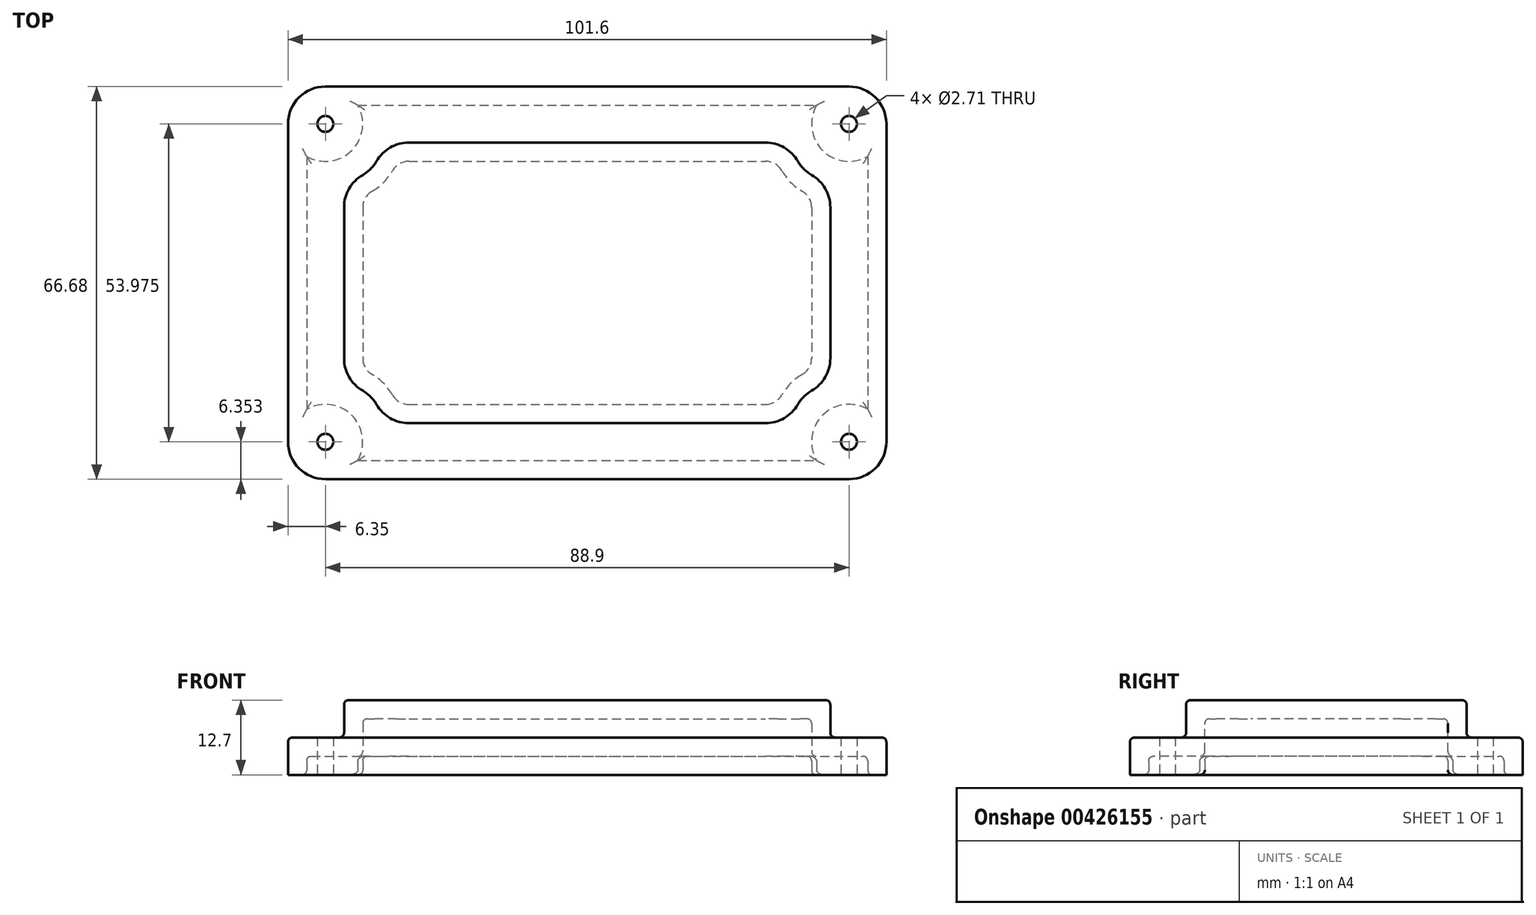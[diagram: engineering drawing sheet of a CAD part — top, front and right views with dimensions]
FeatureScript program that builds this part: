
annotation { "Feature Type Name" : "Feature", "Feature Type Description" : "" }
export const myFeature = defineFeature(function(context is Context, id is Id, definition is map)
    precondition{}
    {
        {
            var Q0;
            Q0=qCreatedBy(makeId("Top.planeOp"),FACE);
            var sketch = newSketch(context, id + "F0", { "sketchPlane" : qUnion([Q0])});
            skLineSegment(sketch, "E0.bottom", {"start": v(-44.45, 33.34) * mm, "end": v(44.45, 33.34) * mm});
            skLineSegment(sketch, "E0.top", {"start": v(-44.45, -33.34) * mm, "end": v(44.45, -33.34) * mm});
            skLineSegment(sketch, "E0.left", {"start": v(-50.8, 26.99) * mm, "end": v(-50.8, -26.99) * mm});
            skLineSegment(sketch, "E0.right", {"start": v(50.8, 26.99) * mm, "end": v(50.8, -26.99) * mm});
            skPoint(sketch, "E0.middle", {"position": v(0, 0) * mm});
            skPoint(sketch, "E1.visualSharp", {"position": v(-50.8, 33.34) * mm});
            skArc(sketch, "E1.filletArc", {"start": v(-44.45, 33.34) * mm, "mid": v(-48.94, 31.48) * mm, "end": v(-50.8, 26.99) * mm});
            skPoint(sketch, "E2.visualSharp", {"position": v(-50.8, -33.34) * mm});
            skArc(sketch, "E2.filletArc", {"start": v(-50.8, -26.99) * mm, "mid": v(-48.94, -31.48) * mm, "end": v(-44.45, -33.34) * mm});
            skPoint(sketch, "E3.visualSharp", {"position": v(50.8, -33.34) * mm});
            skArc(sketch, "E3.filletArc", {"start": v(44.45, -33.34) * mm, "mid": v(48.94, -31.48) * mm, "end": v(50.8, -26.99) * mm});
            skPoint(sketch, "E4.visualSharp", {"position": v(50.8, 33.34) * mm});
            skArc(sketch, "E4.filletArc", {"start": v(50.8, 26.99) * mm, "mid": v(48.94, 31.48) * mm, "end": v(44.45, 33.34) * mm});
            skSolve(sketch);
        }
        {
            var Q0;
            Q0 = qSketchRegion(id + "F0", true);
            extrude(context, id + "F1", {"entities" : qUnion([Q0]), "depth" : 6.35 * mm});
        }
        {
            var Q0;
            Q0=makeQuery(id+"F1.opExtrude","CAP_FACE",FACE,{"disambiguationData":[OSD([sQuery(id+"F0.wireOp",EDGE,"E0.bottom"),sQuery(id+"F0.wireOp",EDGE,"E0.top"),sQuery(id+"F0.wireOp",EDGE,"E0.left"),sQuery(id+"F0.wireOp",EDGE,"E0.right"),sQuery(id+"F0.wireOp",EDGE,"E1.filletArc"),sQuery(id+"F0.wireOp",EDGE,"E2.filletArc"),sQuery(id+"F0.wireOp",EDGE,"E3.filletArc"),sQuery(id+"F0.wireOp",EDGE,"E4.filletArc")])],"isStart":false});
            var sketch = newSketch(context, id + "F2", { "sketchPlane" : qUnion([Q0])});
            skLineSegment(sketch, "E5.0", {"start": v(-41.27, 23.81) * mm, "end": v(-41.28, -23.81) * mm});
            skLineSegment(sketch, "E5.1", {"start": v(-41.27, 23.81) * mm, "end": v(41.28, 23.81) * mm});
            skLineSegment(sketch, "E5.2", {"start": v(41.28, 23.81) * mm, "end": v(41.27, -23.81) * mm});
            skLineSegment(sketch, "E5.3", {"start": v(-41.28, -23.81) * mm, "end": v(41.27, -23.81) * mm});
            skSolve(sketch);
        }
        {
            var Q0;
            Q0 = qSketchRegion(id + "F2", true);
            extrude(context, id + "F3", {"entities" : qUnion([Q0]), "operationType" : NewBodyOperationType.ADD, "depth" : 6.35 * mm});
        }
        {
            var Q0;
            Q0=makeQuery(id+"F3.opExtrude","CAP_FACE",FACE,{"disambiguationData":[OSD([sQuery(id+"F2.wireOp",EDGE,"E5.0"),sQuery(id+"F2.wireOp",EDGE,"E5.1"),sQuery(id+"F2.wireOp",EDGE,"E5.2"),sQuery(id+"F2.wireOp",EDGE,"E5.3")])],"isStart":false});
            var sketch = newSketch(context, id + "F4", { "sketchPlane" : qUnion([Q0])});
            skLineSegment(sketch, "E6", {"start": v(0, 23.81) * mm, "end": v(0, 0) * mm, "construction": true});
            skLineSegment(sketch, "E7", {"start": v(0, 0) * mm, "end": v(41.28, 0) * mm, "construction": true});
            skCircle(sketch, "E8", {"center": v(41.28, 23.81) * mm, "radius": 6.35 * mm});
            skCircle(sketch, "E9.MirrorC", {"center": v(41.28, -23.81) * mm, "radius": 6.35 * mm});
            skSolve(sketch);
        }
        {
            var Q0;
            Q0 = qSketchRegion(id + "F4", true);
            var Q1;
            Q1=makeQuery(id+"F1.opExtrude","CAP_FACE",FACE,{"disambiguationData":[OSD([sQuery(id+"F0.wireOp",EDGE,"E0.bottom"),sQuery(id+"F0.wireOp",EDGE,"E0.top"),sQuery(id+"F0.wireOp",EDGE,"E0.left"),sQuery(id+"F0.wireOp",EDGE,"E0.right"),sQuery(id+"F0.wireOp",EDGE,"E1.filletArc"),sQuery(id+"F0.wireOp",EDGE,"E2.filletArc"),sQuery(id+"F0.wireOp",EDGE,"E3.filletArc"),sQuery(id+"F0.wireOp",EDGE,"E4.filletArc")])],"isStart":false});
            extrude(context, id + "F5", {"entities" : qUnion([Q0]), "operationType" : NewBodyOperationType.REMOVE, "endBound" : BoundingType.UP_TO_SURFACE, "oppositeDirection" : true, "endBoundEntityFace" : qUnion([Q1]), "depth" : 25.4 * mm});
        }
        {
            var Q0;
            Q0=makeQuery(id+"F3.opExtrude","CAP_FACE",FACE,{"disambiguationData":[OSD([sQuery(id+"F2.wireOp",EDGE,"E5.0"),sQuery(id+"F2.wireOp",EDGE,"E5.1"),sQuery(id+"F2.wireOp",EDGE,"E5.2"),sQuery(id+"F2.wireOp",EDGE,"E5.3")])],"isStart":false});
            var sketch = newSketch(context, id + "F6", { "sketchPlane" : qUnion([Q0])});
            skLineSegment(sketch, "E10", {"start": v(0, 23.81) * mm, "end": v(0, 0) * mm, "construction": true});
            skLineSegment(sketch, "E11", {"start": v(0, 0) * mm, "end": v(-41.28, 0) * mm, "construction": true});
            skCircle(sketch, "E12", {"center": v(-41.27, 23.81) * mm, "radius": 6.35 * mm});
            skCircle(sketch, "E13.MirrorC", {"center": v(-41.27, -23.81) * mm, "radius": 6.35 * mm});
            skSolve(sketch);
        }
        {
            var Q0;
            Q0 = qSketchRegion(id + "F6", true);
            var Q1;
            {var subQ0=sQuery(id+"F4.wireOp",EDGE,"E9.MirrorC");var subQ1=makeQuery(id+"F3.opExtrude","CAP_EDGE",EDGE,{"disambiguationData":[OSD([sQuery(id+"F2.wireOp",EDGE,"E5.2")])],"isStart":false});var subQ2=sQuery(id+"F0.wireOp",EDGE,"E4.filletArc");var subQ3=sQuery(id+"F0.wireOp",EDGE,"E3.filletArc");var subQ4=sQuery(id+"F0.wireOp",EDGE,"E2.filletArc");var subQ5=sQuery(id+"F0.wireOp",EDGE,"E1.filletArc");var subQ6=sQuery(id+"F0.wireOp",EDGE,"E0.right");var subQ7=sQuery(id+"F0.wireOp",EDGE,"E0.left");var subQ8=sQuery(id+"F0.wireOp",EDGE,"E0.top");var subQ9=sQuery(id+"F0.wireOp",EDGE,"E0.bottom");var subQ10=sQuery(id+"F4.wireOp",EDGE,"E8");Q1=makeQuery(id+"F5.boolean.opBoolean","MERGE",FACE,{"derivedFrom":[makeQuery(id+"F1.opExtrude","CAP_FACE",FACE,{"disambiguationData":[OSD([subQ9,subQ8,subQ7,subQ6,subQ5,subQ4,subQ3,subQ2])],"isStart":false}),makeQuery(id+"F5.opExtrude","CAP_FACE",FACE,{"disambiguationData":[OSD([subQ9,subQ8,subQ7,subQ6,subQ5,subQ4,subQ3,subQ2]),ownerDisambiguation([makeQuery(id+"F4.imprint","IMPRINT",EDGE,{"disambiguationData":[TD([[makeQuery(id+"F4.imprint","INTERSECT",VERTEX,{"derivedFrom":[makeQuery(id+"F3.opExtrude","CAP_EDGE",EDGE,{"disambiguationData":[OSD([sQuery(id+"F2.wireOp",EDGE,"E5.1")])],"isStart":false}),subQ10]}),-1.0]])],"derivedFrom":subQ10})])],"isStart":false}),makeQuery(id+"F5.opExtrude","CAP_FACE",FACE,{"disambiguationData":[OSD([subQ9,subQ8,subQ7,subQ6,subQ5,subQ4,subQ3,subQ2]),ownerDisambiguation([makeQuery(id+"F4.imprint","IMPRINT",EDGE,{"disambiguationData":[TD([[makeQuery(id+"F4.imprint","INTERSECT",VERTEX,{"derivedFrom":[subQ1,subQ0]}),1.0]])],"derivedFrom":subQ0})])],"isStart":false})]});}
            extrude(context, id + "F7", {"entities" : qUnion([Q0]), "operationType" : NewBodyOperationType.REMOVE, "endBound" : BoundingType.UP_TO_SURFACE, "oppositeDirection" : true, "endBoundEntityFace" : qUnion([Q1]), "depth" : 25.4 * mm});
        }
        {
            var Q0;
            Q0=makeQuery(id+"F7.boolean.opBoolean","INTERSECT",EDGE,{"derivedFrom":[makeQuery(id+"F3.opExtrude","SWEPT_FACE",FACE,{"disambiguationData":[OSD([sQuery(id+"F2.wireOp",EDGE,"E5.3")])]}),makeQuery(id+"F7.opExtrude","SWEPT_FACE",FACE,{"disambiguationData":[OSD([sQuery(id+"F6.wireOp",EDGE,"E13.MirrorC")])]})]});
            var Q1;
            Q1=makeQuery(id+"F7.boolean.opBoolean","INTERSECT",EDGE,{"derivedFrom":[makeQuery(id+"F3.opExtrude","SWEPT_FACE",FACE,{"disambiguationData":[OSD([sQuery(id+"F2.wireOp",EDGE,"E5.0")])]}),makeQuery(id+"F7.opExtrude","SWEPT_FACE",FACE,{"disambiguationData":[OSD([sQuery(id+"F6.wireOp",EDGE,"E13.MirrorC")])]})]});
            var Q2;
            Q2=makeQuery(id+"F7.boolean.opBoolean","INTERSECT",EDGE,{"derivedFrom":[makeQuery(id+"F3.opExtrude","SWEPT_FACE",FACE,{"disambiguationData":[OSD([sQuery(id+"F2.wireOp",EDGE,"E5.0")])]}),makeQuery(id+"F7.opExtrude","SWEPT_FACE",FACE,{"disambiguationData":[OSD([sQuery(id+"F6.wireOp",EDGE,"E12")])]})]});
            var Q3;
            Q3=makeQuery(id+"F7.boolean.opBoolean","INTERSECT",EDGE,{"derivedFrom":[makeQuery(id+"F3.opExtrude","SWEPT_FACE",FACE,{"disambiguationData":[OSD([sQuery(id+"F2.wireOp",EDGE,"E5.1")])]}),makeQuery(id+"F7.opExtrude","SWEPT_FACE",FACE,{"disambiguationData":[OSD([sQuery(id+"F6.wireOp",EDGE,"E12")])]})]});
            var Q4;
            Q4=makeQuery(id+"F5.boolean.opBoolean","INTERSECT",EDGE,{"derivedFrom":[makeQuery(id+"F3.opExtrude","SWEPT_FACE",FACE,{"disambiguationData":[OSD([sQuery(id+"F2.wireOp",EDGE,"E5.1")])]}),makeQuery(id+"F5.opExtrude","SWEPT_FACE",FACE,{"disambiguationData":[OSD([sQuery(id+"F4.wireOp",EDGE,"E8")])]})]});
            var Q5;
            Q5=makeQuery(id+"F5.boolean.opBoolean","INTERSECT",EDGE,{"derivedFrom":[makeQuery(id+"F3.opExtrude","SWEPT_FACE",FACE,{"disambiguationData":[OSD([sQuery(id+"F2.wireOp",EDGE,"E5.2")])]}),makeQuery(id+"F5.opExtrude","SWEPT_FACE",FACE,{"disambiguationData":[OSD([sQuery(id+"F4.wireOp",EDGE,"E8")])]})]});
            var Q6;
            Q6=makeQuery(id+"F5.boolean.opBoolean","INTERSECT",EDGE,{"derivedFrom":[makeQuery(id+"F3.opExtrude","SWEPT_FACE",FACE,{"disambiguationData":[OSD([sQuery(id+"F2.wireOp",EDGE,"E5.2")])]}),makeQuery(id+"F5.opExtrude","SWEPT_FACE",FACE,{"disambiguationData":[OSD([sQuery(id+"F4.wireOp",EDGE,"E9.MirrorC")])]})]});
            var Q7;
            Q7=makeQuery(id+"F5.boolean.opBoolean","INTERSECT",EDGE,{"derivedFrom":[makeQuery(id+"F3.opExtrude","SWEPT_FACE",FACE,{"disambiguationData":[OSD([sQuery(id+"F2.wireOp",EDGE,"E5.3")])]}),makeQuery(id+"F5.opExtrude","SWEPT_FACE",FACE,{"disambiguationData":[OSD([sQuery(id+"F4.wireOp",EDGE,"E9.MirrorC")])]})]});
            fillet(context, id + "F8", {"entities" : qUnion([Q0, Q1, Q2, Q3, Q4, Q5, Q6, Q7]), "radius" : 6.35 * mm, "tangentPropagation" : true, "allowEdgeOverflow" : false});
        }
        {
            var Q0;
            Q0=makeQuery(id+"F1.opExtrude","CAP_FACE",FACE,{"disambiguationData":[OSD([sQuery(id+"F0.wireOp",EDGE,"E0.bottom"),sQuery(id+"F0.wireOp",EDGE,"E0.top"),sQuery(id+"F0.wireOp",EDGE,"E0.left"),sQuery(id+"F0.wireOp",EDGE,"E0.right"),sQuery(id+"F0.wireOp",EDGE,"E1.filletArc"),sQuery(id+"F0.wireOp",EDGE,"E2.filletArc"),sQuery(id+"F0.wireOp",EDGE,"E3.filletArc"),sQuery(id+"F0.wireOp",EDGE,"E4.filletArc")])],"isStart":true});
            shell(context, id + "F9", {"entities" : qUnion([Q0]), "thickness" : 3.17 * mm});
        }
        {
            var Q0;
            Q0=makeQuery(id+"F1.opExtrude","CAP_FACE",FACE,{"disambiguationData":[OSD([sQuery(id+"F0.wireOp",EDGE,"E0.bottom"),sQuery(id+"F0.wireOp",EDGE,"E0.top"),sQuery(id+"F0.wireOp",EDGE,"E0.left"),sQuery(id+"F0.wireOp",EDGE,"E0.right"),sQuery(id+"F0.wireOp",EDGE,"E1.filletArc"),sQuery(id+"F0.wireOp",EDGE,"E2.filletArc"),sQuery(id+"F0.wireOp",EDGE,"E3.filletArc"),sQuery(id+"F0.wireOp",EDGE,"E4.filletArc")])],"isStart":true});
            var sketch = newSketch(context, id + "F10", { "sketchPlane" : qUnion([Q0])});
            skCircle(sketch, "E14", {"center": v(44.45, 26.99) * mm, "radius": 6.35 * mm});
            skCircle(sketch, "E15", {"center": v(44.45, -26.99) * mm, "radius": 6.35 * mm});
            skCircle(sketch, "E16", {"center": v(-44.45, -26.99) * mm, "radius": 6.35 * mm});
            skCircle(sketch, "E17", {"center": v(-44.45, 26.99) * mm, "radius": 6.35 * mm});
            skSolve(sketch);
        }
        {
            var Q0;
            Q0 = qSketchRegion(id + "F10", true);
            var Q1;
            Q1=makeQuery(id+"F9.opShell","OFFSET_FACE",FACE,{"disambiguationData":[OSD([sQuery(id+"F0.wireOp",EDGE,"E0.bottom"),sQuery(id+"F0.wireOp",EDGE,"E0.top"),sQuery(id+"F0.wireOp",EDGE,"E0.left"),sQuery(id+"F0.wireOp",EDGE,"E0.right"),sQuery(id+"F0.wireOp",EDGE,"E1.filletArc"),sQuery(id+"F0.wireOp",EDGE,"E2.filletArc"),sQuery(id+"F0.wireOp",EDGE,"E3.filletArc"),sQuery(id+"F0.wireOp",EDGE,"E4.filletArc")])]});
            extrude(context, id + "F11", {"entities" : qUnion([Q0]), "operationType" : NewBodyOperationType.ADD, "endBound" : BoundingType.UP_TO_SURFACE, "oppositeDirection" : true, "endBoundEntityFace" : qUnion([Q1]), "depth" : 4.57 * mm});
        }
        {
            var Q0;
            Q0=makeQuery(id+"F9.opShell","OFFSET_FACE",FACE,{"disambiguationData":[OSD([sQuery(id+"F0.wireOp",EDGE,"E0.bottom"),sQuery(id+"F0.wireOp",EDGE,"E0.top"),sQuery(id+"F0.wireOp",EDGE,"E0.left"),sQuery(id+"F0.wireOp",EDGE,"E0.right"),sQuery(id+"F0.wireOp",EDGE,"E1.filletArc"),sQuery(id+"F0.wireOp",EDGE,"E2.filletArc"),sQuery(id+"F0.wireOp",EDGE,"E3.filletArc"),sQuery(id+"F0.wireOp",EDGE,"E4.filletArc")])]});
            var Q1;
            Q1=makeQuery(id+"F9.opShell","OFFSET_FACE",FACE,{"disambiguationData":[OSD([sQuery(id+"F2.wireOp",EDGE,"E5.0"),sQuery(id+"F2.wireOp",EDGE,"E5.1"),sQuery(id+"F2.wireOp",EDGE,"E5.2"),sQuery(id+"F2.wireOp",EDGE,"E5.3")])]});
            var Q2;
            {var subQ0=sQuery(id+"F0.wireOp",EDGE,"E0.left");Q2=makeQuery(id+"F9.opShell","OFFSET_EDGE",EDGE,{"disambiguationData":[OSD([subQ0]),TDD([makeQuery(id+"F1.opExtrude","CAP_EDGE",EDGE,{"disambiguationData":[OSD([subQ0])],"isStart":true})])]});}
            var Q3;
            {var subQ0=sQuery(id+"F0.wireOp",EDGE,"E0.bottom");Q3=makeQuery(id+"F9.opShell","OFFSET_EDGE",EDGE,{"disambiguationData":[OSD([subQ0]),TDD([makeQuery(id+"F1.opExtrude","CAP_EDGE",EDGE,{"disambiguationData":[OSD([subQ0])],"isStart":true})])]});}
            var Q4;
            {var subQ0=sQuery(id+"F0.wireOp",EDGE,"E0.right");Q4=makeQuery(id+"F9.opShell","OFFSET_EDGE",EDGE,{"disambiguationData":[OSD([subQ0]),TDD([makeQuery(id+"F1.opExtrude","CAP_EDGE",EDGE,{"disambiguationData":[OSD([subQ0])],"isStart":true})])]});}
            var Q5;
            Q5=makeQuery(id+"F11.opExtrude","CAP_EDGE",EDGE,{"disambiguationData":[OSD([sQuery(id+"F10.wireOp",EDGE,"E15")])],"isStart":true});
            var Q6;
            Q6=makeQuery(id+"F11.opExtrude","CAP_EDGE",EDGE,{"disambiguationData":[OSD([sQuery(id+"F10.wireOp",EDGE,"E14")])],"isStart":true});
            var Q7;
            {var subQ0=sQuery(id+"F0.wireOp",EDGE,"E0.top");Q7=makeQuery(id+"F9.opShell","OFFSET_EDGE",EDGE,{"disambiguationData":[OSD([subQ0]),TDD([makeQuery(id+"F1.opExtrude","CAP_EDGE",EDGE,{"disambiguationData":[OSD([subQ0])],"isStart":true})])]});}
            var Q8;
            Q8=makeQuery(id+"F11.opExtrude","CAP_EDGE",EDGE,{"disambiguationData":[OSD([sQuery(id+"F10.wireOp",EDGE,"E17")])],"isStart":true});
            var Q9;
            Q9=makeQuery(id+"F3.opExtrude","CAP_FACE",FACE,{"disambiguationData":[OSD([sQuery(id+"F2.wireOp",EDGE,"E5.0"),sQuery(id+"F2.wireOp",EDGE,"E5.1"),sQuery(id+"F2.wireOp",EDGE,"E5.2"),sQuery(id+"F2.wireOp",EDGE,"E5.3")])],"isStart":false});
            var Q10;
            {var subQ0=sQuery(id+"F6.wireOp",EDGE,"E13.MirrorC");var subQ1=makeQuery(id+"F3.opExtrude","CAP_EDGE",EDGE,{"disambiguationData":[OSD([sQuery(id+"F2.wireOp",EDGE,"E5.0")])],"isStart":false});var subQ3=sQuery(id+"F0.wireOp",EDGE,"E4.filletArc");var subQ4=sQuery(id+"F0.wireOp",EDGE,"E3.filletArc");var subQ5=sQuery(id+"F0.wireOp",EDGE,"E2.filletArc");var subQ6=sQuery(id+"F0.wireOp",EDGE,"E1.filletArc");var subQ7=sQuery(id+"F0.wireOp",EDGE,"E0.right");var subQ8=sQuery(id+"F0.wireOp",EDGE,"E0.left");var subQ9=sQuery(id+"F0.wireOp",EDGE,"E0.top");var subQ10=sQuery(id+"F0.wireOp",EDGE,"E0.bottom");var subQ11=sQuery(id+"F6.wireOp",EDGE,"E12");var subQ12=makeQuery(id+"F3.opExtrude","CAP_EDGE",EDGE,{"disambiguationData":[OSD([sQuery(id+"F2.wireOp",EDGE,"E5.1")])],"isStart":false});var subQ13=sQuery(id+"F4.wireOp",EDGE,"E9.MirrorC");var subQ14=makeQuery(id+"F3.opExtrude","CAP_EDGE",EDGE,{"disambiguationData":[OSD([sQuery(id+"F2.wireOp",EDGE,"E5.2")])],"isStart":false});var subQ15=sQuery(id+"F4.wireOp",EDGE,"E8");Q10=makeQuery(id+"F7.boolean.opBoolean","MERGE",FACE,{"derivedFrom":[makeQuery(id+"F5.boolean.opBoolean","MERGE",FACE,{"derivedFrom":[makeQuery(id+"F1.opExtrude","CAP_FACE",FACE,{"disambiguationData":[OSD([subQ10,subQ9,subQ8,subQ7,subQ6,subQ5,subQ4,subQ3])],"isStart":false}),makeQuery(id+"F5.opExtrude","CAP_FACE",FACE,{"disambiguationData":[OSD([subQ10,subQ9,subQ8,subQ7,subQ6,subQ5,subQ4,subQ3]),ownerDisambiguation([makeQuery(id+"F4.imprint","IMPRINT",EDGE,{"disambiguationData":[TD([[makeQuery(id+"F4.imprint","INTERSECT",VERTEX,{"derivedFrom":[subQ12,subQ15]}),-1.0]])],"derivedFrom":subQ15})])],"isStart":false}),makeQuery(id+"F5.opExtrude","CAP_FACE",FACE,{"disambiguationData":[OSD([subQ10,subQ9,subQ8,subQ7,subQ6,subQ5,subQ4,subQ3]),ownerDisambiguation([makeQuery(id+"F4.imprint","IMPRINT",EDGE,{"disambiguationData":[TD([[makeQuery(id+"F4.imprint","INTERSECT",VERTEX,{"derivedFrom":[subQ14,subQ13]}),1.0]])],"derivedFrom":subQ13})])],"isStart":false})]}),makeQuery(id+"F7.opExtrude","CAP_FACE",FACE,{"disambiguationData":[OSD([subQ10,subQ9,subQ8,subQ7,subQ6,subQ5,subQ4,subQ3]),ownerDisambiguation([makeQuery(id+"F6.imprint","IMPRINT",EDGE,{"disambiguationData":[TD([[makeQuery(id+"F6.imprint","INTERSECT",VERTEX,{"derivedFrom":[subQ1,subQ11]}),1.0]])],"derivedFrom":subQ11})])],"isStart":false}),makeQuery(id+"F7.opExtrude","CAP_FACE",FACE,{"disambiguationData":[OSD([subQ10,subQ9,subQ8,subQ7,subQ6,subQ5,subQ4,subQ3]),ownerDisambiguation([makeQuery(id+"F6.imprint","IMPRINT",EDGE,{"disambiguationData":[TD([[makeQuery(id+"F6.imprint","INTERSECT",VERTEX,{"derivedFrom":[subQ1,subQ0]}),1.0]])],"derivedFrom":subQ0})])],"isStart":false})]});}
            var Q11;
            Q11=makeQuery(id+"F11.opExtrude","CAP_EDGE",EDGE,{"disambiguationData":[OSD([sQuery(id+"F10.wireOp",EDGE,"E16")])],"isStart":true});
            fillet(context, id + "F12", {"entities" : qUnion([Q0, Q1, Q2, Q3, Q4, Q5, Q6, Q7, Q8, Q9, Q10, Q11]), "radius" : 0.79 * mm, "tangentPropagation" : true, "allowEdgeOverflow" : false});
        }
        {
            var Q0;
            Q0=makeQuery(id+"F11.boolean.opBoolean","MERGE",FACE,{"derivedFrom":[makeQuery(id+"F1.opExtrude","CAP_FACE",FACE,{"disambiguationData":[OSD([sQuery(id+"F0.wireOp",EDGE,"E0.bottom"),sQuery(id+"F0.wireOp",EDGE,"E0.top"),sQuery(id+"F0.wireOp",EDGE,"E0.left"),sQuery(id+"F0.wireOp",EDGE,"E0.right"),sQuery(id+"F0.wireOp",EDGE,"E1.filletArc"),sQuery(id+"F0.wireOp",EDGE,"E2.filletArc"),sQuery(id+"F0.wireOp",EDGE,"E3.filletArc"),sQuery(id+"F0.wireOp",EDGE,"E4.filletArc")])],"isStart":true}),makeQuery(id+"F11.opExtrude","CAP_FACE",FACE,{"disambiguationData":[OSD([sQuery(id+"F10.wireOp",EDGE,"E14")])],"isStart":true}),makeQuery(id+"F11.opExtrude","CAP_FACE",FACE,{"disambiguationData":[OSD([sQuery(id+"F10.wireOp",EDGE,"E15")])],"isStart":true}),makeQuery(id+"F11.opExtrude","CAP_FACE",FACE,{"disambiguationData":[OSD([sQuery(id+"F10.wireOp",EDGE,"E16")])],"isStart":true}),makeQuery(id+"F11.opExtrude","CAP_FACE",FACE,{"disambiguationData":[OSD([sQuery(id+"F10.wireOp",EDGE,"E17")])],"isStart":true})]});
            var sketch = newSketch(context, id + "F13", { "sketchPlane" : qUnion([Q0])});
            skPoint(sketch, "E18", {"position": v(-44.45, 26.99) * mm});
            skPoint(sketch, "E19", {"position": v(-44.45, -26.99) * mm});
            skPoint(sketch, "E20", {"position": v(44.45, -26.99) * mm});
            skPoint(sketch, "E21", {"position": v(44.45, 26.99) * mm});
            skSolve(sketch);
        }
        {
            var Q0;
            Q0=sQuery(id+"F13.wireOp",VERTEX,"E18");
            var Q1;
            Q1=sQuery(id+"F13.wireOp",VERTEX,"E19");
            var Q2;
            Q2=sQuery(id+"F13.wireOp",VERTEX,"E20");
            var Q3;
            Q3=sQuery(id+"F13.wireOp",VERTEX,"E21");
            var Q4;
            Q4=makeQuery(id+"F1.opExtrude","SWEPT_BODY",BODY,{"disambiguationData":[OSD([sQuery(id+"F0.wireOp",EDGE,"E0.bottom"),sQuery(id+"F0.wireOp",EDGE,"E0.top"),sQuery(id+"F0.wireOp",EDGE,"E0.left"),sQuery(id+"F0.wireOp",EDGE,"E0.right"),sQuery(id+"F0.wireOp",EDGE,"E1.filletArc"),sQuery(id+"F0.wireOp",EDGE,"E2.filletArc"),sQuery(id+"F0.wireOp",EDGE,"E3.filletArc"),sQuery(id+"F0.wireOp",EDGE,"E4.filletArc")])]});
            hole(context, id + "F14", {"style" : HoleStyle.SIMPLE, "endStyle" : HoleEndStyle.THROUGH, "standardTappedOrClearance" : lookupTablePath({ "standard" : "ANSI", "engagement" : "75%", "pitch" : "32 tpi", "size" : "#6", "type" : "Tapped" }), "standardBlindInLast" : lookupTablePath({ "standard" : "ANSI", "engagement" : "75%", "pitch" : "32 tpi", "size" : "#6", "type" : "Tapped" }), "holeDiameter" : 2.7 * mm, "showTappedDepth" : true, "tappedDepth" : 17.46 * mm, "tapClearance" : 10, "startFromSketch" : true, "locations" : qUnion([Q0, Q1, Q2, Q3]), "scope" : qUnion([Q4]), "majorDiameter" : 3.5 * mm});
        }
    });
